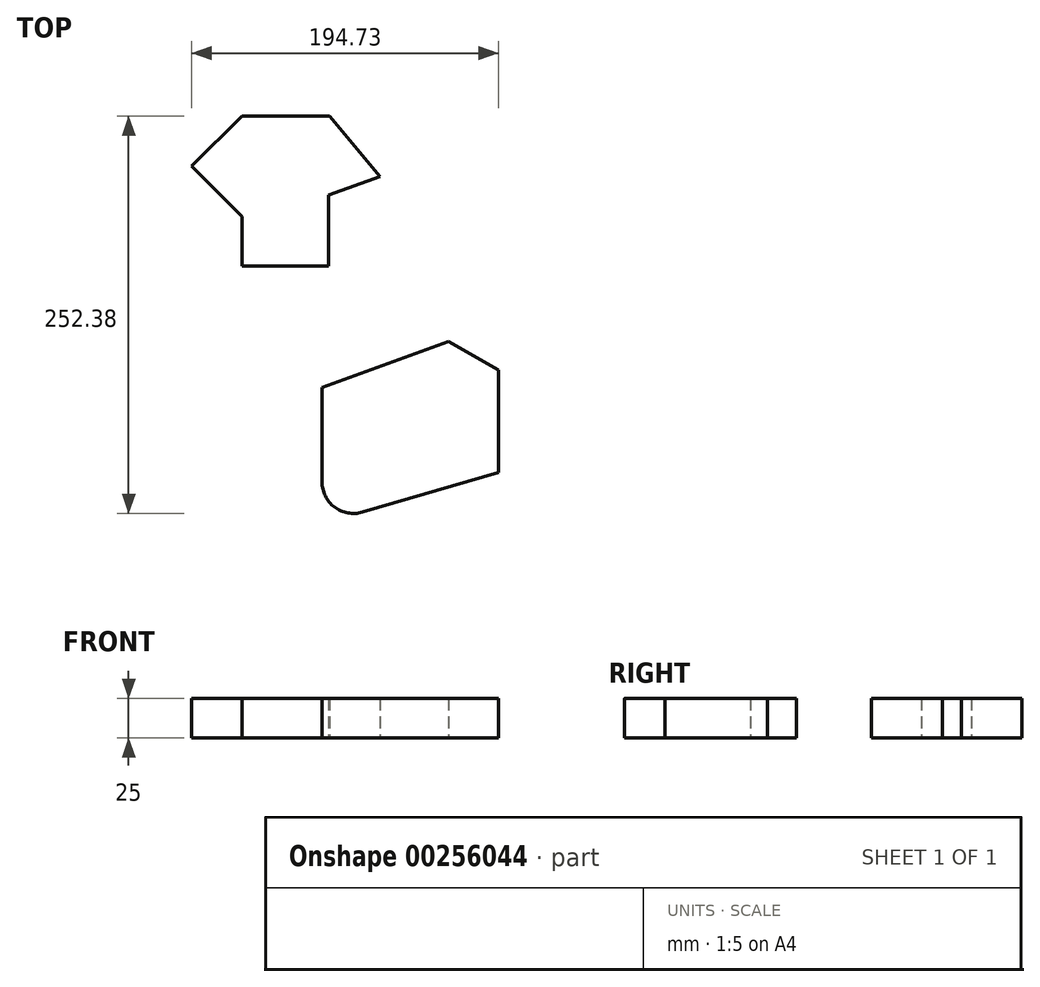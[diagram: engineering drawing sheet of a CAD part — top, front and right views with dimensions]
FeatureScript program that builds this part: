
annotation { "Feature Type Name" : "Feature", "Feature Type Description" : "" }
export const myFeature = defineFeature(function(context is Context, id is Id, definition is map)
    precondition{}
    {
        {
            var Q0;
            Q0=qCreatedBy(makeId("Top.planeOp"),FACE);
            var sketch = newSketch(context, id + "F0", { "sketchPlane" : qUnion([Q0])});
            skLineSegment(sketch, "E0", {"start": v(-33.4, 47.86) * mm, "end": v(21.6, 47.86) * mm});
            skLineSegment(sketch, "E1", {"start": v(21.6, 47.86) * mm, "end": v(21.6, 92.86) * mm});
            skLineSegment(sketch, "E2", {"start": v(21.6, 92.86) * mm, "end": v(54.5, 104.84) * mm});
            skLineSegment(sketch, "E3", {"start": v(54.5, 104.84) * mm, "end": v(22.35, 143.14) * mm});
            skLineSegment(sketch, "E4", {"start": v(22.35, 143.14) * mm, "end": v(-33.4, 143.14) * mm});
            skLineSegment(sketch, "E5", {"start": v(-33.4, 143.14) * mm, "end": v(-65.22, 111.32) * mm});
            skLineSegment(sketch, "E6", {"start": v(-65.22, 111.32) * mm, "end": v(-33.4, 79.5) * mm});
            skLineSegment(sketch, "E7", {"start": v(-33.4, 79.5) * mm, "end": v(-33.4, 47.86) * mm});
            skLineSegment(sketch, "E8", {"start": v(-65.22, 111.32) * mm, "end": v(-23.3, 111.32) * mm});
            skLineSegment(sketch, "E9", {"start": v(129.51, -18.29) * mm, "end": v(129.51, -83.29) * mm});
            skLineSegment(sketch, "E10", {"start": v(129.51, -83.29) * mm, "end": v(43.1, -108.44) * mm});
            skLineSegment(sketch, "E11", {"start": v(17.51, -89.24) * mm, "end": v(17.51, -29.24) * mm});
            skPoint(sketch, "E12.visualSharp", {"position": v(17.51, -115.89) * mm});
            skArc(sketch, "E12.filletArc", {"start": v(17.51, -89.24) * mm, "mid": v(25.5, -105.23) * mm, "end": v(43.1, -108.44) * mm});
            skLineSegment(sketch, "E13", {"start": v(129.51, -18.29) * mm, "end": v(97.84, 0) * mm});
            skLineSegment(sketch, "E14", {"start": v(129.51, -18.29) * mm, "end": v(97.84, -18.29) * mm});
            skLineSegment(sketch, "E15", {"start": v(97.84, 0) * mm, "end": v(17.51, -29.24) * mm});
            skLineSegment(sketch, "E16", {"start": v(17.51, -29.24) * mm, "end": v(70.43, -29.24) * mm});
            skLineSegment(sketch, "E17", {"start": v(70.43, -29.24) * mm, "end": v(64.08, -29.24) * mm});
            skSolve(sketch);
        }
        {
            var Q0;
            Q0 = qSketchRegion(id + "F0", true);
            extrude(context, id + "F1", {"entities" : qUnion([Q0]), "depth" : 25 * mm});
        }
    });
